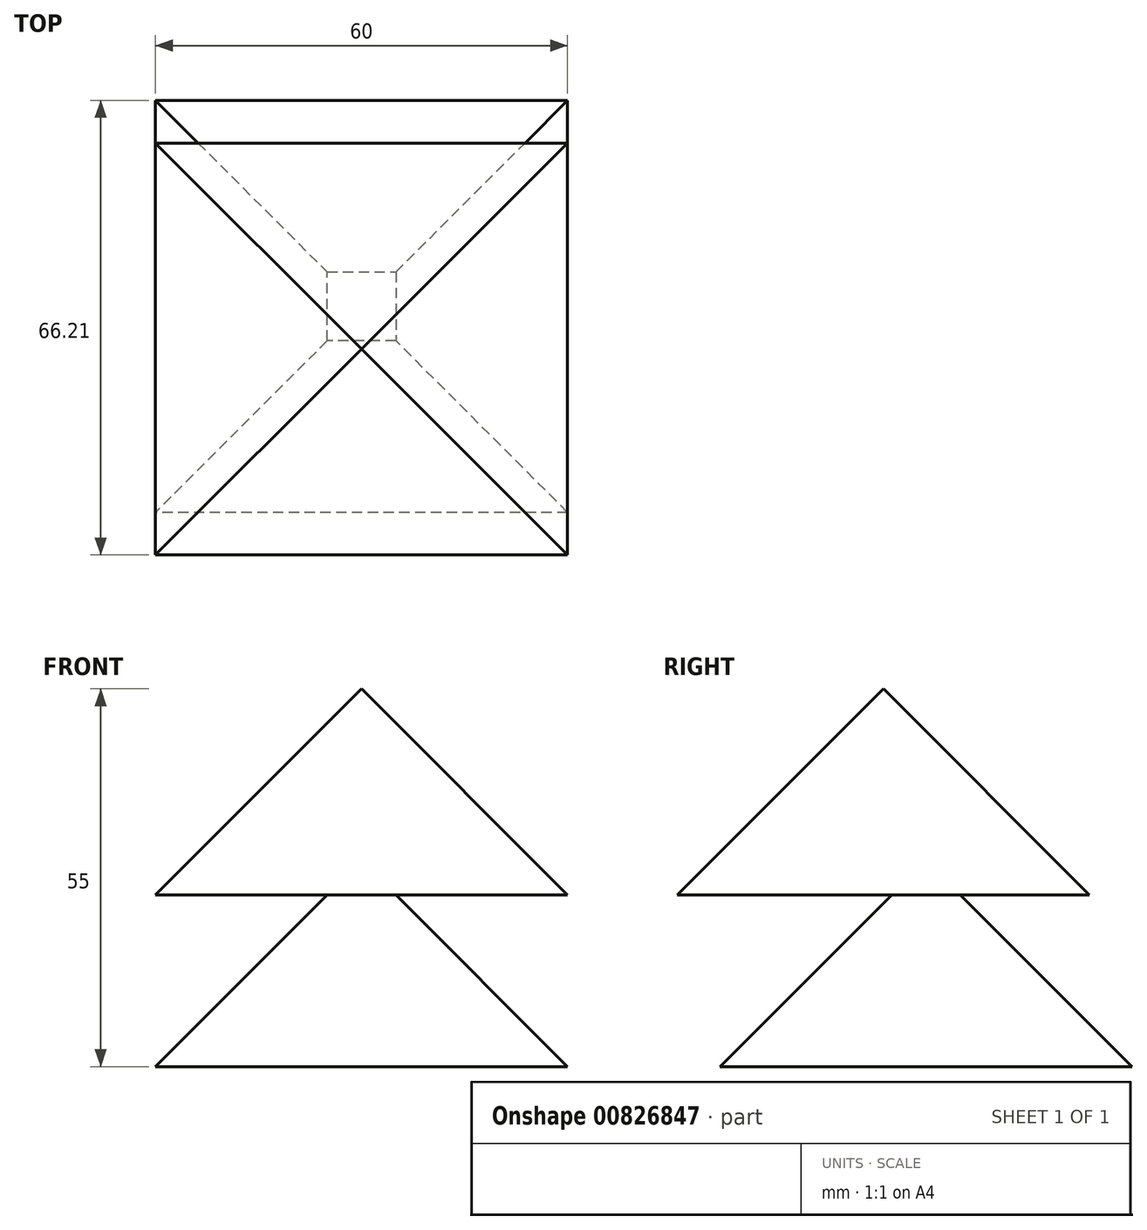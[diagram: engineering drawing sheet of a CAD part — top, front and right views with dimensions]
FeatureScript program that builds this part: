
annotation { "Feature Type Name" : "Feature", "Feature Type Description" : "" }
export const myFeature = defineFeature(function(context is Context, id is Id, definition is map)
    precondition{}
    {
        {
            var Q0;
            Q0=qCreatedBy(makeId("Top.planeOp"),FACE);
            var sketch = newSketch(context, id + "F0", { "sketchPlane" : qUnion([Q0])});
            skLineSegment(sketch, "E0.bottom", {"start": v(-30, 30) * mm, "end": v(30, 30) * mm});
            skLineSegment(sketch, "E0.top", {"start": v(-30, -30) * mm, "end": v(30, -30) * mm});
            skLineSegment(sketch, "E0.left", {"start": v(-30, 30) * mm, "end": v(-30, -30) * mm});
            skLineSegment(sketch, "E0.right", {"start": v(30, 30) * mm, "end": v(30, -30) * mm});
            skPoint(sketch, "E0.middle", {"position": v(0, 0) * mm});
            skSolve(sketch);
        }
        {
            var Q0;
            Q0 = qSketchRegion(id + "F0", true);
            extrude(context, id + "F1", {"entities" : qUnion([Q0]), "depth" : 30 * mm, "offsetDistance" : 25.4 * mm, "hasDraft" : true, "draftAngle" : 45 * degree, "draftPullDirection" : true});
        }
        {
            var Q0;
            Q0=qCreatedBy(makeId("Top.planeOp"),FACE);
            cPlane(context, id + "F2", {"entities" : qUnion([Q0]), "cplaneType" : CPlaneType.OFFSET, "offset" : 25 * mm, "width" : 152.4 * mm, "height" : 152.4 * mm});
        }
        {
            var Q0;
            Q0=qCreatedBy(id+"F2.planeOp",FACE);
            var sketch = newSketch(context, id + "F3", { "sketchPlane" : qUnion([Q0])});
            skLineSegment(sketch, "E1.bottom", {"start": v(30, 23.79) * mm, "end": v(-30, 23.79) * mm});
            skLineSegment(sketch, "E1.top", {"start": v(30, -36.21) * mm, "end": v(-30, -36.21) * mm});
            skLineSegment(sketch, "E1.left", {"start": v(30, 23.79) * mm, "end": v(30, -36.21) * mm});
            skLineSegment(sketch, "E1.right", {"start": v(-30, 23.79) * mm, "end": v(-30, -36.21) * mm});
            skPoint(sketch, "E1.middle", {"position": v(0, -6.21) * mm});
            skSolve(sketch);
        }
        {
            var Q0;
            Q0 = qSketchRegion(id + "F3", true);
            extrude(context, id + "F4", {"entities" : qUnion([Q0]), "operationType" : NewBodyOperationType.ADD, "depth" : 30 * mm, "offsetDistance" : 25.4 * mm, "hasDraft" : true, "draftAngle" : 45 * degree, "draftPullDirection" : true});
        }
    });
